# Revit family: 61087-61087450-glossy_white-400
name_source: partatom
category: Plumbing Fixtures
units: mm (PartAtom-declared; Revit-internal decimal feet)

## family parameters
Always vertical = Yes
Cut with Voids When Loaded = No
OmniClass Number = 23.31.13.00
Part Type = Valve - Breaks Into
Room Calculation Point = No
Round Connector Dimension = Use Diameter
Shared = Yes
Work Plane-Based = No

## types (1)
- Washbasins-hansgrohe-61087XXX-Xevolos E Washbasins Xevolos E Handrinse basin 360_250 with tap hole left without overflow
    ARTNR = 61087450
    BASENUMBER = 61087
    BIMOBJECT = Sanitary: Wash Basins
    CATALOG = Hansgrohe
    DESIGN = Germany
    DO = 46
    DOT = 35
    ETIM = EC011550 | Washbasin
    IFC = Sanitary Terminal
    L = 360
    LI = -162
    LINA = Washbasins-hansgrohe-61087XXX-Xevolos E Washbasins Xevolos E Handrinse basin 360_250 with tap hole left without overflow, SmartClean
    LODLEVEL = 400
    MASTERFORMAT = 22 41 16.13 | Residential Lavatories
    Manufacturer = Hansgrohe
    Model = Washbasins-hansgrohe-61087XXX-Xevolos E Washbasins Xevolos E Handrinse basin 360_250 with tap hole left without overflow, SmartClean
    NAME = Xevolos E Handrinse basin 360_250 with tap hole left without overflow, SmartClean
    NB = 61087-61087450-GLOSSY_WHITE-400
    NBSYN = $BASENUMBER.-$ARTNR.-$SURFACE.-$LODLEVEL.
    NN = Xevolos Washbasin
    OBJECTTYPE = Object (single object)
    OMNICLASS = 23-31 13 00 | Sinks
    PERMALINK = 61087XXX
    PRODUCTFAMILY = Xevolos E
    PRODUCTGROUP = Washbasins
    PRODUCTURL = https://pro.hansgrohe.com
    REGION = Worldwide
    SPECIFICATION = Surfaces:  - 61087450 White   Specification:  • consists of: handrinse basin, waste set, cover  • material: ceramic  • SmartClean: dirt-repellent glaze • degree of gloss: glossy  • ceramic cover included • with one tap hole • without overflow • without shelf • non-closing waste set • 360 x 250 mm • type of installation: wall mounted  • suitable for cabinet
    SURFACE = GLOSSY_WHITE
    TAP = 1
    UNICLASS2015 = Pr_40_20_96 | Wash basins, sinks and troughs
    UNICLASS_2015_CODE = 40_20_96
    UNIFORMATII = D2010 | Plumbing Fixtures
    UNSPSC = 301815 | Sanitary ware
    X1 = 0
    X2 = 0

## geometry (parser evidence)
native form markers: Sweep x6
no freeform markers — native parametric forms only
